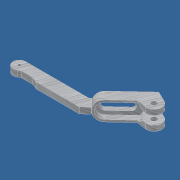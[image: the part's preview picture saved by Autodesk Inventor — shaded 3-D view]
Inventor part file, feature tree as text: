
AUTODESK INVENTOR PART (.ipt)
format: ipt  version: unknown  size: 280,576 bytes
history: native  units: mm
features: extrude x6, sketch x6, mirror x1
ambient origin geometry x8: Origin, YZ Plane, XZ Plane, XY Plane, X Axis, Y Axis, Z Axis, Center Point
feature tree (13):
  extrude  "Выдавливание1"  Depth=1.2mm
  extrude  "Выдавливание2"  Depth=2.6mm
  extrude  "Выдавливание3"  Depth=5.15mm
  extrude  "Выдавливание4"  Depth=4.2mm
  extrude  "Выдавливание5"  Depth=4.9mm
  extrude  "Выдавливание6"  Depth=9.5mm
  mirror  "Зеркальное отражение1"
  sketch  "Эскиз1"
  sketch  "Эскиз2"
  sketch  "Эскиз3"
  sketch  "Эскиз4"
  sketch  "Эскиз5"
  sketch  "Эскиз6"
